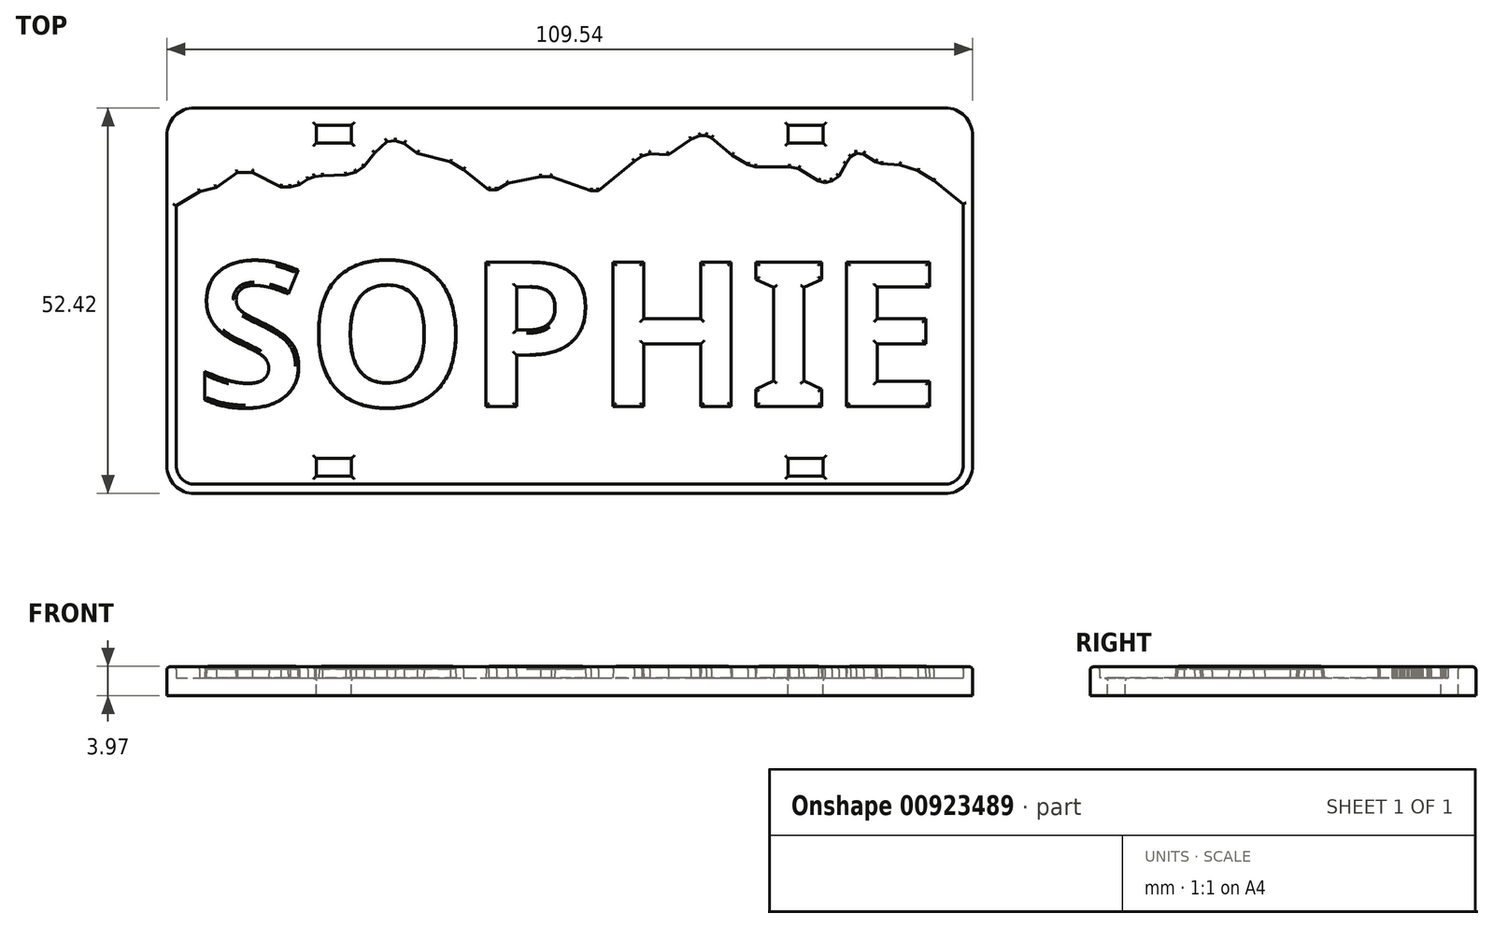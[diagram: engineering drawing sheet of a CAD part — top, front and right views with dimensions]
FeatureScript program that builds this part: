
annotation { "Feature Type Name" : "Feature", "Feature Type Description" : "" }
export const myFeature = defineFeature(function(context is Context, id is Id, definition is map)
    precondition{}
    {
        {
            var Q0;
            Q0=qCreatedBy(makeId("Top.planeOp"),FACE);
            var sketch = newSketch(context, id + "F0", { "sketchPlane" : qUnion([Q0])});
            skLineSegment(sketch, "E0", {"start": v(54.77, -22.46) * mm, "end": v(54.77, 22.46) * mm});
            skArc(sketch, "E1", {"start": v(54.77, 22.46) * mm, "mid": v(53.68, 25.11) * mm, "end": v(51.02, 26.21) * mm});
            skLineSegment(sketch, "E2", {"start": v(51.02, 26.21) * mm, "end": v(-51.02, 26.21) * mm});
            skArc(sketch, "E3", {"start": v(-51.02, 26.21) * mm, "mid": v(-53.68, 25.11) * mm, "end": v(-54.77, 22.46) * mm});
            skLineSegment(sketch, "E4", {"start": v(-54.77, 22.46) * mm, "end": v(-54.77, -22.46) * mm});
            skArc(sketch, "E5", {"start": v(-54.77, -22.46) * mm, "mid": v(-53.54, -25.24) * mm, "end": v(-50.64, -26.2) * mm});
            skLineSegment(sketch, "E6", {"start": v(-50.64, -26.2) * mm, "end": v(51.04, -26.2) * mm});
            skArc(sketch, "E7", {"start": v(51.02, -26.21) * mm, "mid": v(53.68, -25.11) * mm, "end": v(54.77, -22.46) * mm});
            skLineSegment(sketch, "E8", {"start": v(-54.77, 12.13) * mm, "end": v(-50.31, 14.84) * mm});
            skLineSegment(sketch, "E9", {"start": v(-50.31, 14.84) * mm, "end": v(-48.06, 15.4) * mm});
            skLineSegment(sketch, "E10", {"start": v(-48.06, 15.4) * mm, "end": v(-45.2, 17.44) * mm});
            skLineSegment(sketch, "E11", {"start": v(-45.2, 17.44) * mm, "end": v(-43.14, 17.44) * mm});
            skLineSegment(sketch, "E12", {"start": v(-43.14, 17.44) * mm, "end": v(-39.3, 15.5) * mm});
            skLineSegment(sketch, "E13", {"start": v(-39.3, 15.5) * mm, "end": v(-38.03, 15.49) * mm});
            skLineSegment(sketch, "E14", {"start": v(-38.03, 15.49) * mm, "end": v(-36.75, 15.8) * mm});
            skLineSegment(sketch, "E15", {"start": v(-36.75, 15.8) * mm, "end": v(-35.57, 16.54) * mm});
            skLineSegment(sketch, "E16", {"start": v(-35.57, 16.54) * mm, "end": v(-34.73, 16.88) * mm});
            skLineSegment(sketch, "E17", {"start": v(-34.73, 16.88) * mm, "end": v(-33.6, 17.01) * mm});
            skLineSegment(sketch, "E18", {"start": v(-33.6, 17.01) * mm, "end": v(-30.43, 17.11) * mm});
            skLineSegment(sketch, "E19", {"start": v(-29.05, 17.5) * mm, "end": v(-27.98, 18.27) * mm});
            skLineSegment(sketch, "E20", {"start": v(-27.98, 18.27) * mm, "end": v(-26.53, 20.14) * mm});
            skLineSegment(sketch, "E21", {"start": v(-26.53, 20.14) * mm, "end": v(-24.88, 21.63) * mm});
            skLineSegment(sketch, "E22", {"start": v(-24.88, 21.63) * mm, "end": v(-23.73, 21.77) * mm});
            skLineSegment(sketch, "E23", {"start": v(-22.5, 21.4) * mm, "end": v(-20.72, 20.04) * mm});
            skLineSegment(sketch, "E24", {"start": v(-16.23, 18.87) * mm, "end": v(-14.45, 17.85) * mm});
            skLineSegment(sketch, "E25", {"start": v(-14.45, 17.85) * mm, "end": v(-11.02, 15.1) * mm});
            skLineSegment(sketch, "E26", {"start": v(-11.02, 15.1) * mm, "end": v(-9.93, 15.1) * mm});
            skLineSegment(sketch, "E27", {"start": v(-9.93, 15.1) * mm, "end": v(-8.4, 15.96) * mm});
            skLineSegment(sketch, "E28", {"start": v(-8.4, 15.96) * mm, "end": v(-3.94, 16.85) * mm});
            skLineSegment(sketch, "E29", {"start": v(-3.94, 16.85) * mm, "end": v(-2.54, 16.85) * mm});
            skLineSegment(sketch, "E30", {"start": v(-2.54, 16.85) * mm, "end": v(2.9, 14.97) * mm});
            skLineSegment(sketch, "E31", {"start": v(2.9, 14.97) * mm, "end": v(3.92, 14.97) * mm});
            skLineSegment(sketch, "E32", {"start": v(3.92, 14.97) * mm, "end": v(8.8, 18.97) * mm});
            skLineSegment(sketch, "E33", {"start": v(8.8, 18.97) * mm, "end": v(9.82, 19.64) * mm});
            skLineSegment(sketch, "E34", {"start": v(9.82, 19.64) * mm, "end": v(10.9, 19.97) * mm});
            skLineSegment(sketch, "E35", {"start": v(10.9, 19.97) * mm, "end": v(13.43, 19.86) * mm});
            skLineSegment(sketch, "E36", {"start": v(16.5, 21.96) * mm, "end": v(17.71, 22.42) * mm});
            skLineSegment(sketch, "E37", {"start": v(17.71, 22.42) * mm, "end": v(18.56, 22.45) * mm});
            skLineSegment(sketch, "E38", {"start": v(18.56, 22.45) * mm, "end": v(19.28, 22.13) * mm});
            skLineSegment(sketch, "E39", {"start": v(19.28, 22.13) * mm, "end": v(22.05, 19.8) * mm});
            skLineSegment(sketch, "E40", {"start": v(22.05, 19.8) * mm, "end": v(24.2, 18.5) * mm});
            skLineSegment(sketch, "E41", {"start": v(24.2, 18.5) * mm, "end": v(25.23, 18.2) * mm});
            skLineSegment(sketch, "E42", {"start": v(25.23, 18.2) * mm, "end": v(29.85, 18.2) * mm});
            skLineSegment(sketch, "E43", {"start": v(29.85, 18.2) * mm, "end": v(31.13, 17.95) * mm});
            skLineSegment(sketch, "E44", {"start": v(31.13, 17.95) * mm, "end": v(33.84, 16.27) * mm});
            skLineSegment(sketch, "E45", {"start": v(33.84, 16.27) * mm, "end": v(34.73, 16.06) * mm});
            skLineSegment(sketch, "E46", {"start": v(34.73, 16.06) * mm, "end": v(35.67, 16.3) * mm});
            skLineSegment(sketch, "E47", {"start": v(35.67, 16.3) * mm, "end": v(36.58, 16.95) * mm});
            skLineSegment(sketch, "E48", {"start": v(36.58, 16.95) * mm, "end": v(37.58, 18.67) * mm});
            skLineSegment(sketch, "E49", {"start": v(38.22, 19.58) * mm, "end": v(38.96, 20.06) * mm});
            skLineSegment(sketch, "E50", {"start": v(38.96, 20.06) * mm, "end": v(39.94, 19.92) * mm});
            skLineSegment(sketch, "E51", {"start": v(41.58, 18.88) * mm, "end": v(42.4, 18.61) * mm});
            skLineSegment(sketch, "E52", {"start": v(42.4, 18.61) * mm, "end": v(44.9, 18.47) * mm});
            skLineSegment(sketch, "E53", {"start": v(44.9, 18.47) * mm, "end": v(47.31, 17.68) * mm});
            skLineSegment(sketch, "E54", {"start": v(47.31, 17.68) * mm, "end": v(49.47, 16.33) * mm});
            skLineSegment(sketch, "E55", {"start": v(49.47, 16.33) * mm, "end": v(51.88, 14.42) * mm});
            skLineSegment(sketch, "E56", {"start": v(51.88, 14.42) * mm, "end": v(53.78, 12.92) * mm});
            skLineSegment(sketch, "E57", {"start": v(53.78, 12.92) * mm, "end": v(54.77, 12.06) * mm});
            skLineSegment(sketch, "E58", {"start": v(-20.72, 20.04) * mm, "end": v(-16.23, 18.87) * mm});
            skLineSegment(sketch, "E59", {"start": v(16.5, 21.96) * mm, "end": v(13.43, 19.86) * mm});
            skLineSegment(sketch, "E60", {"start": v(-22.5, 21.4) * mm, "end": v(-23.73, 21.77) * mm});
            skLineSegment(sketch, "E61", {"start": v(-29.05, 17.5) * mm, "end": v(-30.43, 17.11) * mm});
            skLineSegment(sketch, "E62", {"start": v(37.58, 18.67) * mm, "end": v(38.22, 19.58) * mm});
            skLineSegment(sketch, "E63", {"start": v(41.58, 18.88) * mm, "end": v(39.94, 19.92) * mm});
            skSolve(sketch);
        }
        {
            var Q0;
            Q0=qCreatedBy(makeId("Top.planeOp"),FACE);
            var sketch = newSketch(context, id + "F1", { "sketchPlane" : qUnion([Q0])});
            skLineSegment(sketch, "E64", {"start": v(54.77, -22.46) * mm, "end": v(54.77, 22.46) * mm});
            skArc(sketch, "E65", {"start": v(54.77, 22.46) * mm, "mid": v(53.68, 25.11) * mm, "end": v(51.02, 26.21) * mm});
            skLineSegment(sketch, "E66", {"start": v(51.02, 26.21) * mm, "end": v(-51.02, 26.21) * mm});
            skArc(sketch, "E67", {"start": v(-51.02, 26.21) * mm, "mid": v(-53.68, 25.11) * mm, "end": v(-54.77, 22.46) * mm});
            skLineSegment(sketch, "E68", {"start": v(-54.77, 22.46) * mm, "end": v(-54.77, -22.46) * mm});
            skArc(sketch, "E69", {"start": v(-54.77, -22.46) * mm, "mid": v(-53.68, -25.11) * mm, "end": v(-51.02, -26.21) * mm});
            skLineSegment(sketch, "E70", {"start": v(-51.02, -26.21) * mm, "end": v(51.02, -26.21) * mm});
            skArc(sketch, "E71", {"start": v(51.02, -26.21) * mm, "mid": v(53.68, -25.11) * mm, "end": v(54.77, -22.46) * mm});
            skLineSegment(sketch, "E72.0", {"start": v(50.96, 24.94) * mm, "end": v(-50.96, 24.94) * mm, "construction": true});
            skLineSegment(sketch, "E72.1", {"start": v(53.5, -22.4) * mm, "end": v(53.5, 22.4) * mm, "construction": true});
            skLineSegment(sketch, "E72.2", {"start": v(-50.96, -24.94) * mm, "end": v(50.96, -24.94) * mm, "construction": true});
            skLineSegment(sketch, "E72.3", {"start": v(-53.5, 22.4) * mm, "end": v(-53.5, -22.4) * mm, "construction": true});
            skPoint(sketch, "E73.visualSharp", {"position": v(-53.5, 24.94) * mm});
            skArc(sketch, "E73.filletArc", {"start": v(-50.96, 24.94) * mm, "mid": v(-52.76, 24.2) * mm, "end": v(-53.5, 22.4) * mm, "construction": true});
            skPoint(sketch, "E74.visualSharp", {"position": v(-53.5, -24.94) * mm});
            skArc(sketch, "E74.filletArc", {"start": v(-53.5, -22.4) * mm, "mid": v(-52.76, -24.2) * mm, "end": v(-50.96, -24.94) * mm, "construction": true});
            skPoint(sketch, "E75.visualSharp", {"position": v(53.5, -24.94) * mm});
            skArc(sketch, "E75.filletArc", {"start": v(50.96, -24.94) * mm, "mid": v(52.76, -24.2) * mm, "end": v(53.5, -22.4) * mm, "construction": true});
            skPoint(sketch, "E76.visualSharp", {"position": v(53.5, 24.94) * mm});
            skArc(sketch, "E76.filletArc", {"start": v(53.5, 22.4) * mm, "mid": v(52.76, 24.2) * mm, "end": v(50.96, 24.94) * mm, "construction": true});
            skSolve(sketch);
        }
        {
            var Q0;
            {var subQ3=sQuery(id+"F0.wireOp",EDGE,"E1");Q0=makeQuery(id+"F0.imprint","IMPRINT",FACE,{"disambiguationData":[TD([[makeQuery(id+"F0.imprint","IMPRINT",EDGE,{"derivedFrom":subQ3}),1.0]])]});}
            extrude(context, id + "F2", {"entities" : qUnion([Q0]), "depth" : 1.52 * mm, "offsetDistance" : 25.4 * mm});
        }
        {
            var Q0;
            Q0=qSketchRegion(id+"F1",true);
            extrude(context, id + "F3", {"entities" : qUnion([Q0]), "operationType" : NewBodyOperationType.ADD, "oppositeDirection" : true, "depth" : 2.38 * mm, "offsetDistance" : 25.4 * mm});
        }
        {
            var Q0;
            {var subQ58=sQuery(id+"F0.wireOp",EDGE,"E0");var subQ59=sQuery(id+"F1.wireOp",EDGE,"E64");var subQ60=sQuery(id+"F1.wireOp",EDGE,"E65");var subQ61=sQuery(id+"F1.wireOp",EDGE,"E68");var subQ62=sQuery(id+"F1.wireOp",EDGE,"E69");var subQ63=sQuery(id+"F1.wireOp",EDGE,"E70");var subQ64=sQuery(id+"F1.wireOp",EDGE,"E71");Q0=makeQuery(id+"F3.boolean.opBoolean","SPLIT",FACE,{"disambiguationData":[TD([makeQuery(id+"F2.opExtrude","SWEPT_FACE",FACE,{"disambiguationData":[OSD([subQ58])]})])],"derivedFrom":makeQuery(id+"F3.opExtrude","CAP_FACE",FACE,{"disambiguationData":[OSD([subQ59,subQ60,sQuery(id+"F1.wireOp",EDGE,"E66"),sQuery(id+"F1.wireOp",EDGE,"E67"),subQ61,subQ62,subQ63,subQ64])],"isStart":true})});}
            var sketch = newSketch(context, id + "F4", { "sketchPlane" : qUnion([Q0])});
            skLineSegment(sketch, "E77", {"start": v(54.77, -22.46) * mm, "end": v(54.77, 12.06) * mm});
            skLineSegment(sketch, "E78", {"start": v(-54.77, 12.13) * mm, "end": v(-54.77, -22.46) * mm});
            skArc(sketch, "E79", {"start": v(-54.77, -22.46) * mm, "mid": v(-53.68, -25.11) * mm, "end": v(-51.02, -26.21) * mm});
            skLineSegment(sketch, "E80", {"start": v(-51.02, -26.21) * mm, "end": v(51.02, -26.21) * mm});
            skArc(sketch, "E81", {"start": v(51.02, -26.21) * mm, "mid": v(53.68, -25.11) * mm, "end": v(54.77, -22.46) * mm});
            skLineSegment(sketch, "E82.1", {"start": v(53.5, -22.4) * mm, "end": v(53.5, 13.14) * mm});
            skLineSegment(sketch, "E82.2", {"start": v(-50.96, -24.94) * mm, "end": v(50.96, -24.94) * mm});
            skLineSegment(sketch, "E82.3", {"start": v(-53.5, 12.9) * mm, "end": v(-53.5, -22.4) * mm});
            skPoint(sketch, "E83.visualSharp", {"position": v(-53.5, 24.94) * mm});
            skPoint(sketch, "E84.visualSharp", {"position": v(-53.5, -24.94) * mm});
            skArc(sketch, "E84.filletArc", {"start": v(-53.5, -22.4) * mm, "mid": v(-52.76, -24.2) * mm, "end": v(-50.96, -24.94) * mm});
            skPoint(sketch, "E85.visualSharp", {"position": v(53.5, -24.94) * mm});
            skArc(sketch, "E85.filletArc", {"start": v(50.96, -24.94) * mm, "mid": v(52.76, -24.2) * mm, "end": v(53.5, -22.4) * mm});
            skPoint(sketch, "E86.visualSharp", {"position": v(53.5, 24.94) * mm});
            skLineSegment(sketch, "E87", {"start": v(-54.77, 12.13) * mm, "end": v(-53.5, 12.9) * mm});
            skLineSegment(sketch, "E88", {"start": v(53.5, 13.14) * mm, "end": v(53.78, 12.92) * mm});
            skLineSegment(sketch, "E89", {"start": v(53.78, 12.92) * mm, "end": v(54.77, 12.06) * mm});
            skSolve(sketch);
        }
        {
            var Q0;
            Q0=qSketchRegion(id+"F4",true);
            extrude(context, id + "F5", {"entities" : qUnion([Q0]), "operationType" : NewBodyOperationType.ADD, "depth" : 1.52 * mm, "offsetDistance" : 25.4 * mm});
        }
        {
            var Q0;
            Q0=makeQuery(id+"F5.boolean.opBoolean","MERGE",FACE,{"derivedFrom":[makeQuery(id+"F2.opExtrude","CAP_FACE",FACE,{"disambiguationData":[OSD([sQuery(id+"F0.wireOp",EDGE,"E0"),sQuery(id+"F0.wireOp",EDGE,"E1"),sQuery(id+"F0.wireOp",EDGE,"E2"),sQuery(id+"F0.wireOp",EDGE,"E3"),sQuery(id+"F0.wireOp",EDGE,"E4"),sQuery(id+"F0.wireOp",EDGE,"E8"),sQuery(id+"F0.wireOp",EDGE,"E9"),sQuery(id+"F0.wireOp",EDGE,"E10"),sQuery(id+"F0.wireOp",EDGE,"E11"),sQuery(id+"F0.wireOp",EDGE,"E12"),sQuery(id+"F0.wireOp",EDGE,"E13"),sQuery(id+"F0.wireOp",EDGE,"E14"),sQuery(id+"F0.wireOp",EDGE,"E15"),sQuery(id+"F0.wireOp",EDGE,"E16"),sQuery(id+"F0.wireOp",EDGE,"E17"),sQuery(id+"F0.wireOp",EDGE,"E18"),sQuery(id+"F0.wireOp",EDGE,"7b9f405e-0691-426e-9c9e-a5372cf0836a"),sQuery(id+"F0.wireOp",EDGE,"E19"),sQuery(id+"F0.wireOp",EDGE,"E20"),sQuery(id+"F0.wireOp",EDGE,"E21"),sQuery(id+"F0.wireOp",EDGE,"E22"),sQuery(id+"F0.wireOp",EDGE,"b3dec5b1-662c-4d50-a13c-af7b7760114a"),sQuery(id+"F0.wireOp",EDGE,"E23"),sQuery(id+"F0.wireOp",EDGE,"4d9ee76e-0833-4cdc-b1a8-2d4ce76e6521"),sQuery(id+"F0.wireOp",EDGE,"E24"),sQuery(id+"F0.wireOp",EDGE,"E25"),sQuery(id+"F0.wireOp",EDGE,"E26"),sQuery(id+"F0.wireOp",EDGE,"E27"),sQuery(id+"F0.wireOp",EDGE,"E28"),sQuery(id+"F0.wireOp",EDGE,"E29"),sQuery(id+"F0.wireOp",EDGE,"E30"),sQuery(id+"F0.wireOp",EDGE,"E31"),sQuery(id+"F0.wireOp",EDGE,"E32"),sQuery(id+"F0.wireOp",EDGE,"E33"),sQuery(id+"F0.wireOp",EDGE,"E34"),sQuery(id+"F0.wireOp",EDGE,"E35"),sQuery(id+"F0.wireOp",EDGE,"55551997-bb9e-4b94-90c5-def3cb147476"),sQuery(id+"F0.wireOp",EDGE,"E36"),sQuery(id+"F0.wireOp",EDGE,"E37"),sQuery(id+"F0.wireOp",EDGE,"E38"),sQuery(id+"F0.wireOp",EDGE,"E39"),sQuery(id+"F0.wireOp",EDGE,"E40"),sQuery(id+"F0.wireOp",EDGE,"E41"),sQuery(id+"F0.wireOp",EDGE,"E42"),sQuery(id+"F0.wireOp",EDGE,"E43"),sQuery(id+"F0.wireOp",EDGE,"E44"),sQuery(id+"F0.wireOp",EDGE,"E45"),sQuery(id+"F0.wireOp",EDGE,"E46"),sQuery(id+"F0.wireOp",EDGE,"E47"),sQuery(id+"F0.wireOp",EDGE,"E48"),sQuery(id+"F0.wireOp",EDGE,"513b7cbe-d979-4e22-b277-f3c42ccdbda1"),sQuery(id+"F0.wireOp",EDGE,"E49"),sQuery(id+"F0.wireOp",EDGE,"E50"),sQuery(id+"F0.wireOp",EDGE,"0d842e13-672c-40e3-aae4-28923e78d4e0"),sQuery(id+"F0.wireOp",EDGE,"E51"),sQuery(id+"F0.wireOp",EDGE,"E52"),sQuery(id+"F0.wireOp",EDGE,"E53"),sQuery(id+"F0.wireOp",EDGE,"E54"),sQuery(id+"F0.wireOp",EDGE,"E55"),sQuery(id+"F0.wireOp",EDGE,"E56"),sQuery(id+"F0.wireOp",EDGE,"E57")])],"isStart":false}),makeQuery(id+"F5.opExtrude","CAP_FACE",FACE,{"disambiguationData":[OSD([sQuery(id+"F4.wireOp",EDGE,"E77"),sQuery(id+"F4.wireOp",EDGE,"E78"),sQuery(id+"F4.wireOp",EDGE,"E79"),sQuery(id+"F4.wireOp",EDGE,"E80"),sQuery(id+"F4.wireOp",EDGE,"E81"),sQuery(id+"F4.wireOp",EDGE,"E82.1"),sQuery(id+"F4.wireOp",EDGE,"E82.2"),sQuery(id+"F4.wireOp",EDGE,"E82.3"),sQuery(id+"F4.wireOp",EDGE,"E84.filletArc"),sQuery(id+"F4.wireOp",EDGE,"E85.filletArc"),sQuery(id+"F4.wireOp",EDGE,"E87"),sQuery(id+"F4.wireOp",EDGE,"E88"),sQuery(id+"F4.wireOp",EDGE,"E89")])],"isStart":false})]});
            var sketch = newSketch(context, id + "F6", { "sketchPlane" : qUnion([Q0])});
            skLineSegment(sketch, "E90.bottom", {"start": v(-34.45, 23.83) * mm, "end": v(-29.7, 23.83) * mm});
            skLineSegment(sketch, "E90.top", {"start": v(-34.45, 21.45) * mm, "end": v(-29.7, 21.45) * mm});
            skLineSegment(sketch, "E90.left", {"start": v(-34.45, 23.83) * mm, "end": v(-34.45, 21.45) * mm});
            skLineSegment(sketch, "E90.right", {"start": v(-29.7, 23.83) * mm, "end": v(-29.7, 21.45) * mm});
            skLineSegment(sketch, "E91", {"start": v(0, 26.21) * mm, "end": v(0, -26.21) * mm, "construction": true});
            skLineSegment(sketch, "E92.MirrorCS", {"start": v(34.45, 23.83) * mm, "end": v(34.45, 21.45) * mm});
            skLineSegment(sketch, "E93.MirrorCS", {"start": v(29.7, 23.83) * mm, "end": v(29.7, 21.45) * mm});
            skLineSegment(sketch, "E94.MirrorCS", {"start": v(34.45, 21.45) * mm, "end": v(29.7, 21.45) * mm});
            skLineSegment(sketch, "E95.MirrorCS", {"start": v(34.45, 23.83) * mm, "end": v(29.7, 23.83) * mm});
            skLineSegment(sketch, "E96", {"start": v(0, 0) * mm, "end": v(-59.23, 0) * mm, "construction": true});
            skLineSegment(sketch, "E97", {"start": v(0, 0) * mm, "end": v(56.47, 0) * mm, "construction": true});
            skLineSegment(sketch, "E98.MirrorCS", {"start": v(-34.45, -23.83) * mm, "end": v(-29.7, -23.83) * mm});
            skLineSegment(sketch, "E99.MirrorCS", {"start": v(-34.45, -23.83) * mm, "end": v(-34.45, -21.45) * mm});
            skLineSegment(sketch, "E100.MirrorCS", {"start": v(-34.45, -21.45) * mm, "end": v(-29.7, -21.45) * mm});
            skLineSegment(sketch, "E101.MirrorCS", {"start": v(-29.7, -23.83) * mm, "end": v(-29.7, -21.45) * mm});
            skLineSegment(sketch, "E102.MirrorCS", {"start": v(29.7, -23.83) * mm, "end": v(29.7, -21.45) * mm});
            skLineSegment(sketch, "E103.MirrorCS", {"start": v(34.45, -23.83) * mm, "end": v(29.7, -23.83) * mm});
            skLineSegment(sketch, "E104.MirrorCS", {"start": v(34.45, -23.83) * mm, "end": v(34.45, -21.45) * mm});
            skLineSegment(sketch, "E105.MirrorCS", {"start": v(34.45, -21.45) * mm, "end": v(29.7, -21.45) * mm});
            skSolve(sketch);
        }
        {
            var Q0;
            Q0=qSketchRegion(id+"F6",true);
            extrude(context, id + "F7", {"entities" : qUnion([Q0]), "operationType" : NewBodyOperationType.REMOVE, "endBound" : BoundingType.THROUGH_ALL, "oppositeDirection" : true, "depth" : 25.4 * mm, "offsetDistance" : 25.4 * mm});
        }
        {
            var Q0;
            Q0=makeQuery(id+"F3.opExtrude","CAP_FACE",FACE,{"disambiguationData":[OSD([sQuery(id+"F1.wireOp",EDGE,"E64"),sQuery(id+"F1.wireOp",EDGE,"E65"),sQuery(id+"F1.wireOp",EDGE,"E66"),sQuery(id+"F1.wireOp",EDGE,"E67"),sQuery(id+"F1.wireOp",EDGE,"E68"),sQuery(id+"F1.wireOp",EDGE,"E69"),sQuery(id+"F1.wireOp",EDGE,"E70"),sQuery(id+"F1.wireOp",EDGE,"E71")])],"isStart":true});
            var sketch = newSketch(context, id + "F8", { "sketchPlane" : qUnion([Q0])});
            skText(sketch, "E106", { "text": "SOPHIE", "fontName": "NotoSans-Bold.ttf"});
            const initialGuessF8  = {"E106": [-0.0509, -0.01437, 1, 0, 0.0198]};
            skSetInitialGuess(sketch, initialGuessF8);
            skSolve(sketch);
        }
        {
            var Q0;
            Q0=qSketchRegion(id+"F8",true);
            extrude(context, id + "F9", {"entities" : qUnion([Q0]), "operationType" : NewBodyOperationType.ADD, "depth" : 1.59 * mm, "offsetDistance" : 25.4 * mm, "hasDraft" : true, "draftAngle" : 3 * degree, "draftPullDirection" : true});
        }
        {
            var Q0;
            Q0=makeQuery(id+"F5.boolean.opBoolean","MERGE",FACE,{"derivedFrom":[makeQuery(id+"F2.opExtrude","CAP_FACE",FACE,{"disambiguationData":[OSD([sQuery(id+"F0.wireOp",EDGE,"E0"),sQuery(id+"F0.wireOp",EDGE,"E1"),sQuery(id+"F0.wireOp",EDGE,"E2"),sQuery(id+"F0.wireOp",EDGE,"E3"),sQuery(id+"F0.wireOp",EDGE,"E4"),sQuery(id+"F0.wireOp",EDGE,"E8"),sQuery(id+"F0.wireOp",EDGE,"E9"),sQuery(id+"F0.wireOp",EDGE,"E10"),sQuery(id+"F0.wireOp",EDGE,"E11"),sQuery(id+"F0.wireOp",EDGE,"E12"),sQuery(id+"F0.wireOp",EDGE,"E13"),sQuery(id+"F0.wireOp",EDGE,"E14"),sQuery(id+"F0.wireOp",EDGE,"E15"),sQuery(id+"F0.wireOp",EDGE,"E16"),sQuery(id+"F0.wireOp",EDGE,"E17"),sQuery(id+"F0.wireOp",EDGE,"E18"),sQuery(id+"F0.wireOp",EDGE,"7b9f405e-0691-426e-9c9e-a5372cf0836a"),sQuery(id+"F0.wireOp",EDGE,"E19"),sQuery(id+"F0.wireOp",EDGE,"E20"),sQuery(id+"F0.wireOp",EDGE,"E21"),sQuery(id+"F0.wireOp",EDGE,"E22"),sQuery(id+"F0.wireOp",EDGE,"b3dec5b1-662c-4d50-a13c-af7b7760114a"),sQuery(id+"F0.wireOp",EDGE,"E23"),sQuery(id+"F0.wireOp",EDGE,"4d9ee76e-0833-4cdc-b1a8-2d4ce76e6521"),sQuery(id+"F0.wireOp",EDGE,"E24"),sQuery(id+"F0.wireOp",EDGE,"E25"),sQuery(id+"F0.wireOp",EDGE,"E26"),sQuery(id+"F0.wireOp",EDGE,"E27"),sQuery(id+"F0.wireOp",EDGE,"E28"),sQuery(id+"F0.wireOp",EDGE,"E29"),sQuery(id+"F0.wireOp",EDGE,"E30"),sQuery(id+"F0.wireOp",EDGE,"E31"),sQuery(id+"F0.wireOp",EDGE,"E32"),sQuery(id+"F0.wireOp",EDGE,"E33"),sQuery(id+"F0.wireOp",EDGE,"E34"),sQuery(id+"F0.wireOp",EDGE,"E35"),sQuery(id+"F0.wireOp",EDGE,"55551997-bb9e-4b94-90c5-def3cb147476"),sQuery(id+"F0.wireOp",EDGE,"E36"),sQuery(id+"F0.wireOp",EDGE,"E37"),sQuery(id+"F0.wireOp",EDGE,"E38"),sQuery(id+"F0.wireOp",EDGE,"E39"),sQuery(id+"F0.wireOp",EDGE,"E40"),sQuery(id+"F0.wireOp",EDGE,"E41"),sQuery(id+"F0.wireOp",EDGE,"E42"),sQuery(id+"F0.wireOp",EDGE,"E43"),sQuery(id+"F0.wireOp",EDGE,"E44"),sQuery(id+"F0.wireOp",EDGE,"E45"),sQuery(id+"F0.wireOp",EDGE,"E46"),sQuery(id+"F0.wireOp",EDGE,"E47"),sQuery(id+"F0.wireOp",EDGE,"E48"),sQuery(id+"F0.wireOp",EDGE,"513b7cbe-d979-4e22-b277-f3c42ccdbda1"),sQuery(id+"F0.wireOp",EDGE,"E49"),sQuery(id+"F0.wireOp",EDGE,"E50"),sQuery(id+"F0.wireOp",EDGE,"0d842e13-672c-40e3-aae4-28923e78d4e0"),sQuery(id+"F0.wireOp",EDGE,"E51"),sQuery(id+"F0.wireOp",EDGE,"E52"),sQuery(id+"F0.wireOp",EDGE,"E53"),sQuery(id+"F0.wireOp",EDGE,"E54"),sQuery(id+"F0.wireOp",EDGE,"E55"),sQuery(id+"F0.wireOp",EDGE,"E56"),sQuery(id+"F0.wireOp",EDGE,"E57")])],"isStart":false}),makeQuery(id+"F5.opExtrude","CAP_FACE",FACE,{"disambiguationData":[OSD([sQuery(id+"F4.wireOp",EDGE,"E77"),sQuery(id+"F4.wireOp",EDGE,"E78"),sQuery(id+"F4.wireOp",EDGE,"E79"),sQuery(id+"F4.wireOp",EDGE,"E80"),sQuery(id+"F4.wireOp",EDGE,"E81"),sQuery(id+"F4.wireOp",EDGE,"E82.1"),sQuery(id+"F4.wireOp",EDGE,"E82.2"),sQuery(id+"F4.wireOp",EDGE,"E82.3"),sQuery(id+"F4.wireOp",EDGE,"E84.filletArc"),sQuery(id+"F4.wireOp",EDGE,"E85.filletArc"),sQuery(id+"F4.wireOp",EDGE,"E87"),sQuery(id+"F4.wireOp",EDGE,"E88"),sQuery(id+"F4.wireOp",EDGE,"E89")])],"isStart":false})]});
            var Q1;
            {var subQ0=sQuery(id+"F1.wireOp",EDGE,"E64");var subQ1=sQuery(id+"F1.wireOp",EDGE,"E68");var subQ2=sQuery(id+"F1.wireOp",EDGE,"E69");var subQ3=sQuery(id+"F1.wireOp",EDGE,"E70");var subQ4=sQuery(id+"F1.wireOp",EDGE,"E71");Q1=makeQuery(id+"F7.boolean.opBoolean","INTERSECT",EDGE,{"derivedFrom":[makeQuery(id+"F3.boolean.opBoolean","SPLIT",FACE,{"disambiguationData":[TD([makeQuery(id+"F2.opExtrude","SWEPT_FACE",FACE,{"disambiguationData":[OSD([sQuery(id+"F0.wireOp",EDGE,"E0")])]})])],"derivedFrom":makeQuery(id+"F3.opExtrude","CAP_FACE",FACE,{"disambiguationData":[OSD([subQ0,sQuery(id+"F1.wireOp",EDGE,"E65"),sQuery(id+"F1.wireOp",EDGE,"E66"),sQuery(id+"F1.wireOp",EDGE,"E67"),subQ1,subQ2,subQ3,subQ4])],"isStart":true})}),makeQuery(id+"F7.opExtrude","SWEPT_FACE",FACE,{"disambiguationData":[OSD([sQuery(id+"F6.wireOp",EDGE,"E100.MirrorCS")])]})]});}
            var Q2;
            {var subQ0=sQuery(id+"F1.wireOp",EDGE,"E64");var subQ1=sQuery(id+"F1.wireOp",EDGE,"E68");var subQ2=sQuery(id+"F1.wireOp",EDGE,"E69");var subQ3=sQuery(id+"F1.wireOp",EDGE,"E70");var subQ4=sQuery(id+"F1.wireOp",EDGE,"E71");Q2=makeQuery(id+"F7.boolean.opBoolean","INTERSECT",EDGE,{"derivedFrom":[makeQuery(id+"F3.boolean.opBoolean","SPLIT",FACE,{"disambiguationData":[TD([makeQuery(id+"F2.opExtrude","SWEPT_FACE",FACE,{"disambiguationData":[OSD([sQuery(id+"F0.wireOp",EDGE,"E0")])]})])],"derivedFrom":makeQuery(id+"F3.opExtrude","CAP_FACE",FACE,{"disambiguationData":[OSD([subQ0,sQuery(id+"F1.wireOp",EDGE,"E65"),sQuery(id+"F1.wireOp",EDGE,"E66"),sQuery(id+"F1.wireOp",EDGE,"E67"),subQ1,subQ2,subQ3,subQ4])],"isStart":true})}),makeQuery(id+"F7.opExtrude","SWEPT_FACE",FACE,{"disambiguationData":[OSD([sQuery(id+"F6.wireOp",EDGE,"E99.MirrorCS")])]})]});}
            var Q3;
            {var subQ0=sQuery(id+"F1.wireOp",EDGE,"E64");var subQ1=sQuery(id+"F1.wireOp",EDGE,"E68");var subQ2=sQuery(id+"F1.wireOp",EDGE,"E69");var subQ3=sQuery(id+"F1.wireOp",EDGE,"E70");var subQ4=sQuery(id+"F1.wireOp",EDGE,"E71");Q3=makeQuery(id+"F7.boolean.opBoolean","INTERSECT",EDGE,{"derivedFrom":[makeQuery(id+"F3.boolean.opBoolean","SPLIT",FACE,{"disambiguationData":[TD([makeQuery(id+"F2.opExtrude","SWEPT_FACE",FACE,{"disambiguationData":[OSD([sQuery(id+"F0.wireOp",EDGE,"E0")])]})])],"derivedFrom":makeQuery(id+"F3.opExtrude","CAP_FACE",FACE,{"disambiguationData":[OSD([subQ0,sQuery(id+"F1.wireOp",EDGE,"E65"),sQuery(id+"F1.wireOp",EDGE,"E66"),sQuery(id+"F1.wireOp",EDGE,"E67"),subQ1,subQ2,subQ3,subQ4])],"isStart":true})}),makeQuery(id+"F7.opExtrude","SWEPT_FACE",FACE,{"disambiguationData":[OSD([sQuery(id+"F6.wireOp",EDGE,"E98.MirrorCS")])]})]});}
            var Q4;
            {var subQ0=sQuery(id+"F1.wireOp",EDGE,"E64");var subQ1=sQuery(id+"F1.wireOp",EDGE,"E68");var subQ2=sQuery(id+"F1.wireOp",EDGE,"E69");var subQ3=sQuery(id+"F1.wireOp",EDGE,"E70");var subQ4=sQuery(id+"F1.wireOp",EDGE,"E71");Q4=makeQuery(id+"F7.boolean.opBoolean","INTERSECT",EDGE,{"derivedFrom":[makeQuery(id+"F3.boolean.opBoolean","SPLIT",FACE,{"disambiguationData":[TD([makeQuery(id+"F2.opExtrude","SWEPT_FACE",FACE,{"disambiguationData":[OSD([sQuery(id+"F0.wireOp",EDGE,"E0")])]})])],"derivedFrom":makeQuery(id+"F3.opExtrude","CAP_FACE",FACE,{"disambiguationData":[OSD([subQ0,sQuery(id+"F1.wireOp",EDGE,"E65"),sQuery(id+"F1.wireOp",EDGE,"E66"),sQuery(id+"F1.wireOp",EDGE,"E67"),subQ1,subQ2,subQ3,subQ4])],"isStart":true})}),makeQuery(id+"F7.opExtrude","SWEPT_FACE",FACE,{"disambiguationData":[OSD([sQuery(id+"F6.wireOp",EDGE,"E101.MirrorCS")])]})]});}
            var Q5;
            {var subQ0=sQuery(id+"F1.wireOp",EDGE,"E64");var subQ1=sQuery(id+"F1.wireOp",EDGE,"E68");var subQ2=sQuery(id+"F1.wireOp",EDGE,"E69");var subQ3=sQuery(id+"F1.wireOp",EDGE,"E70");var subQ4=sQuery(id+"F1.wireOp",EDGE,"E71");Q5=makeQuery(id+"F7.boolean.opBoolean","INTERSECT",EDGE,{"derivedFrom":[makeQuery(id+"F3.boolean.opBoolean","SPLIT",FACE,{"disambiguationData":[TD([makeQuery(id+"F2.opExtrude","SWEPT_FACE",FACE,{"disambiguationData":[OSD([sQuery(id+"F0.wireOp",EDGE,"E0")])]})])],"derivedFrom":makeQuery(id+"F3.opExtrude","CAP_FACE",FACE,{"disambiguationData":[OSD([subQ0,sQuery(id+"F1.wireOp",EDGE,"E65"),sQuery(id+"F1.wireOp",EDGE,"E66"),sQuery(id+"F1.wireOp",EDGE,"E67"),subQ1,subQ2,subQ3,subQ4])],"isStart":true})}),makeQuery(id+"F7.opExtrude","SWEPT_FACE",FACE,{"disambiguationData":[OSD([sQuery(id+"F6.wireOp",EDGE,"E102.MirrorCS")])]})]});}
            var Q6;
            {var subQ0=sQuery(id+"F1.wireOp",EDGE,"E64");var subQ1=sQuery(id+"F1.wireOp",EDGE,"E68");var subQ2=sQuery(id+"F1.wireOp",EDGE,"E69");var subQ3=sQuery(id+"F1.wireOp",EDGE,"E70");var subQ4=sQuery(id+"F1.wireOp",EDGE,"E71");Q6=makeQuery(id+"F7.boolean.opBoolean","INTERSECT",EDGE,{"derivedFrom":[makeQuery(id+"F3.boolean.opBoolean","SPLIT",FACE,{"disambiguationData":[TD([makeQuery(id+"F2.opExtrude","SWEPT_FACE",FACE,{"disambiguationData":[OSD([sQuery(id+"F0.wireOp",EDGE,"E0")])]})])],"derivedFrom":makeQuery(id+"F3.opExtrude","CAP_FACE",FACE,{"disambiguationData":[OSD([subQ0,sQuery(id+"F1.wireOp",EDGE,"E65"),sQuery(id+"F1.wireOp",EDGE,"E66"),sQuery(id+"F1.wireOp",EDGE,"E67"),subQ1,subQ2,subQ3,subQ4])],"isStart":true})}),makeQuery(id+"F7.opExtrude","SWEPT_FACE",FACE,{"disambiguationData":[OSD([sQuery(id+"F6.wireOp",EDGE,"E105.MirrorCS")])]})]});}
            var Q7;
            {var subQ0=sQuery(id+"F1.wireOp",EDGE,"E64");var subQ1=sQuery(id+"F1.wireOp",EDGE,"E68");var subQ2=sQuery(id+"F1.wireOp",EDGE,"E69");var subQ3=sQuery(id+"F1.wireOp",EDGE,"E70");var subQ4=sQuery(id+"F1.wireOp",EDGE,"E71");Q7=makeQuery(id+"F7.boolean.opBoolean","INTERSECT",EDGE,{"derivedFrom":[makeQuery(id+"F3.boolean.opBoolean","SPLIT",FACE,{"disambiguationData":[TD([makeQuery(id+"F2.opExtrude","SWEPT_FACE",FACE,{"disambiguationData":[OSD([sQuery(id+"F0.wireOp",EDGE,"E0")])]})])],"derivedFrom":makeQuery(id+"F3.opExtrude","CAP_FACE",FACE,{"disambiguationData":[OSD([subQ0,sQuery(id+"F1.wireOp",EDGE,"E65"),sQuery(id+"F1.wireOp",EDGE,"E66"),sQuery(id+"F1.wireOp",EDGE,"E67"),subQ1,subQ2,subQ3,subQ4])],"isStart":true})}),makeQuery(id+"F7.opExtrude","SWEPT_FACE",FACE,{"disambiguationData":[OSD([sQuery(id+"F6.wireOp",EDGE,"E104.MirrorCS")])]})]});}
            var Q8;
            {var subQ0=sQuery(id+"F1.wireOp",EDGE,"E64");var subQ1=sQuery(id+"F1.wireOp",EDGE,"E68");var subQ2=sQuery(id+"F1.wireOp",EDGE,"E69");var subQ3=sQuery(id+"F1.wireOp",EDGE,"E70");var subQ4=sQuery(id+"F1.wireOp",EDGE,"E71");Q8=makeQuery(id+"F7.boolean.opBoolean","INTERSECT",EDGE,{"derivedFrom":[makeQuery(id+"F3.boolean.opBoolean","SPLIT",FACE,{"disambiguationData":[TD([makeQuery(id+"F2.opExtrude","SWEPT_FACE",FACE,{"disambiguationData":[OSD([sQuery(id+"F0.wireOp",EDGE,"E0")])]})])],"derivedFrom":makeQuery(id+"F3.opExtrude","CAP_FACE",FACE,{"disambiguationData":[OSD([subQ0,sQuery(id+"F1.wireOp",EDGE,"E65"),sQuery(id+"F1.wireOp",EDGE,"E66"),sQuery(id+"F1.wireOp",EDGE,"E67"),subQ1,subQ2,subQ3,subQ4])],"isStart":true})}),makeQuery(id+"F7.opExtrude","SWEPT_FACE",FACE,{"disambiguationData":[OSD([sQuery(id+"F6.wireOp",EDGE,"E103.MirrorCS")])]})]});}
            var Q9;
            Q9=makeQuery(id+"F9.opExtrude","CAP_FACE",FACE,{"disambiguationData":[OSD([sQuery(id+"F8.wireOp",EDGE,"E106.sketch_text.stroke-0"),sQuery(id+"F8.wireOp",EDGE,"E106.sketch_text.stroke-1"),sQuery(id+"F8.wireOp",EDGE,"E106.sketch_text.stroke-2"),sQuery(id+"F8.wireOp",EDGE,"E106.sketch_text.stroke-3"),sQuery(id+"F8.wireOp",EDGE,"E106.sketch_text.stroke-4"),sQuery(id+"F8.wireOp",EDGE,"E106.sketch_text.stroke-5"),sQuery(id+"F8.wireOp",EDGE,"E106.sketch_text.stroke-6"),sQuery(id+"F8.wireOp",EDGE,"E106.sketch_text.stroke-7"),sQuery(id+"F8.wireOp",EDGE,"E106.sketch_text.stroke-8"),sQuery(id+"F8.wireOp",EDGE,"E106.sketch_text.stroke-9"),sQuery(id+"F8.wireOp",EDGE,"E106.sketch_text.stroke-10"),sQuery(id+"F8.wireOp",EDGE,"E106.sketch_text.stroke-11"),sQuery(id+"F8.wireOp",EDGE,"E106.sketch_text.stroke-12"),sQuery(id+"F8.wireOp",EDGE,"E106.sketch_text.stroke-13"),sQuery(id+"F8.wireOp",EDGE,"E106.sketch_text.stroke-14")])],"isStart":false});
            var Q10;
            Q10=makeQuery(id+"F9.opExtrude","CAP_FACE",FACE,{"disambiguationData":[OSD([sQuery(id+"F8.wireOp",EDGE,"E106.sketch_text.stroke-15"),sQuery(id+"F8.wireOp",EDGE,"E106.sketch_text.stroke-16"),sQuery(id+"F8.wireOp",EDGE,"E106.sketch_text.stroke-17"),sQuery(id+"F8.wireOp",EDGE,"E106.sketch_text.stroke-18"),sQuery(id+"F8.wireOp",EDGE,"E106.sketch_text.stroke-19"),sQuery(id+"F8.wireOp",EDGE,"E106.sketch_text.stroke-20"),sQuery(id+"F8.wireOp",EDGE,"E106.sketch_text.stroke-21"),sQuery(id+"F8.wireOp",EDGE,"E106.sketch_text.stroke-22"),sQuery(id+"F8.wireOp",EDGE,"E106.sketch_text.stroke-23"),sQuery(id+"F8.wireOp",EDGE,"E106.sketch_text.stroke-24"),sQuery(id+"F8.wireOp",EDGE,"E106.sketch_text.stroke-25"),sQuery(id+"F8.wireOp",EDGE,"E106.sketch_text.stroke-26"),sQuery(id+"F8.wireOp",EDGE,"E106.sketch_text.stroke-27"),sQuery(id+"F8.wireOp",EDGE,"E106.sketch_text.stroke-28")])],"isStart":false});
            var Q11;
            Q11=makeQuery(id+"F9.opExtrude","CAP_FACE",FACE,{"disambiguationData":[OSD([sQuery(id+"F8.wireOp",EDGE,"E106.sketch_text.stroke-29"),sQuery(id+"F8.wireOp",EDGE,"E106.sketch_text.stroke-30"),sQuery(id+"F8.wireOp",EDGE,"E106.sketch_text.stroke-31"),sQuery(id+"F8.wireOp",EDGE,"E106.sketch_text.stroke-32"),sQuery(id+"F8.wireOp",EDGE,"E106.sketch_text.stroke-33"),sQuery(id+"F8.wireOp",EDGE,"E106.sketch_text.stroke-34"),sQuery(id+"F8.wireOp",EDGE,"E106.sketch_text.stroke-35"),sQuery(id+"F8.wireOp",EDGE,"E106.sketch_text.stroke-36"),sQuery(id+"F8.wireOp",EDGE,"E106.sketch_text.stroke-37"),sQuery(id+"F8.wireOp",EDGE,"E106.sketch_text.stroke-38"),sQuery(id+"F8.wireOp",EDGE,"E106.sketch_text.stroke-39"),sQuery(id+"F8.wireOp",EDGE,"E106.sketch_text.stroke-40"),sQuery(id+"F8.wireOp",EDGE,"E106.sketch_text.stroke-41"),sQuery(id+"F8.wireOp",EDGE,"E106.sketch_text.stroke-42")])],"isStart":false});
            var Q12;
            Q12=makeQuery(id+"F9.opExtrude","CAP_FACE",FACE,{"disambiguationData":[OSD([sQuery(id+"F8.wireOp",EDGE,"E106.sketch_text.stroke-57"),sQuery(id+"F8.wireOp",EDGE,"E106.sketch_text.stroke-58"),sQuery(id+"F8.wireOp",EDGE,"E106.sketch_text.stroke-59"),sQuery(id+"F8.wireOp",EDGE,"E106.sketch_text.stroke-60"),sQuery(id+"F8.wireOp",EDGE,"E106.sketch_text.stroke-61"),sQuery(id+"F8.wireOp",EDGE,"E106.sketch_text.stroke-62"),sQuery(id+"F8.wireOp",EDGE,"E106.sketch_text.stroke-63"),sQuery(id+"F8.wireOp",EDGE,"E106.sketch_text.stroke-64"),sQuery(id+"F8.wireOp",EDGE,"E106.sketch_text.stroke-65"),sQuery(id+"F8.wireOp",EDGE,"E106.sketch_text.stroke-66"),sQuery(id+"F8.wireOp",EDGE,"E106.sketch_text.stroke-67"),sQuery(id+"F8.wireOp",EDGE,"E106.sketch_text.stroke-68"),sQuery(id+"F8.wireOp",EDGE,"E106.sketch_text.stroke-69"),sQuery(id+"F8.wireOp",EDGE,"E106.sketch_text.stroke-70")])],"isStart":false});
            var Q13;
            Q13=makeQuery(id+"F9.opExtrude","CAP_FACE",FACE,{"disambiguationData":[OSD([sQuery(id+"F8.wireOp",EDGE,"E106.sketch_text.stroke-71"),sQuery(id+"F8.wireOp",EDGE,"E106.sketch_text.stroke-72"),sQuery(id+"F8.wireOp",EDGE,"E106.sketch_text.stroke-73"),sQuery(id+"F8.wireOp",EDGE,"E106.sketch_text.stroke-74"),sQuery(id+"F8.wireOp",EDGE,"E106.sketch_text.stroke-75"),sQuery(id+"F8.wireOp",EDGE,"E106.sketch_text.stroke-76"),sQuery(id+"F8.wireOp",EDGE,"E106.sketch_text.stroke-77"),sQuery(id+"F8.wireOp",EDGE,"E106.sketch_text.stroke-78"),sQuery(id+"F8.wireOp",EDGE,"E106.sketch_text.stroke-79"),sQuery(id+"F8.wireOp",EDGE,"E106.sketch_text.stroke-80"),sQuery(id+"F8.wireOp",EDGE,"E106.sketch_text.stroke-81"),sQuery(id+"F8.wireOp",EDGE,"E106.sketch_text.stroke-82"),sQuery(id+"F8.wireOp",EDGE,"E106.sketch_text.stroke-83"),sQuery(id+"F8.wireOp",EDGE,"E106.sketch_text.stroke-84"),sQuery(id+"F8.wireOp",EDGE,"E106.sketch_text.stroke-85"),sQuery(id+"F8.wireOp",EDGE,"E106.sketch_text.stroke-86"),sQuery(id+"F8.wireOp",EDGE,"E106.sketch_text.stroke-87"),sQuery(id+"F8.wireOp",EDGE,"E106.sketch_text.stroke-88"),sQuery(id+"F8.wireOp",EDGE,"E106.sketch_text.stroke-89")])],"isStart":false});
            var Q14;
            Q14=makeQuery(id+"F9.opExtrude","CAP_FACE",FACE,{"disambiguationData":[OSD([sQuery(id+"F8.wireOp",EDGE,"E106.sketch_text.stroke-43"),sQuery(id+"F8.wireOp",EDGE,"E106.sketch_text.stroke-44"),sQuery(id+"F8.wireOp",EDGE,"E106.sketch_text.stroke-45"),sQuery(id+"F8.wireOp",EDGE,"E106.sketch_text.stroke-46"),sQuery(id+"F8.wireOp",EDGE,"E106.sketch_text.stroke-47"),sQuery(id+"F8.wireOp",EDGE,"E106.sketch_text.stroke-48"),sQuery(id+"F8.wireOp",EDGE,"E106.sketch_text.stroke-49"),sQuery(id+"F8.wireOp",EDGE,"E106.sketch_text.stroke-50"),sQuery(id+"F8.wireOp",EDGE,"E106.sketch_text.stroke-51"),sQuery(id+"F8.wireOp",EDGE,"E106.sketch_text.stroke-52"),sQuery(id+"F8.wireOp",EDGE,"E106.sketch_text.stroke-53"),sQuery(id+"F8.wireOp",EDGE,"E106.sketch_text.stroke-54"),sQuery(id+"F8.wireOp",EDGE,"E106.sketch_text.stroke-55"),sQuery(id+"F8.wireOp",EDGE,"E106.sketch_text.stroke-56")])],"isStart":false});
            var Q15;
            Q15=makeQuery(id+"F9.opExtrude","CAP_FACE",FACE,{"disambiguationData":[OSD([sQuery(id+"F8.wireOp",EDGE,"E106.sketch_text.stroke-12"),sQuery(id+"F8.wireOp",EDGE,"E106.sketch_text.stroke-13"),sQuery(id+"F8.wireOp",EDGE,"E106.sketch_text.stroke-14"),sQuery(id+"F8.wireOp",EDGE,"E106.sketch_text.stroke-15"),sQuery(id+"F8.wireOp",EDGE,"E106.sketch_text.stroke-16"),sQuery(id+"F8.wireOp",EDGE,"E106.sketch_text.stroke-17")])],"isStart":false});
            var Q16;
            Q16=makeQuery(id+"F9.opExtrude","CAP_FACE",FACE,{"disambiguationData":[OSD([sQuery(id+"F8.wireOp",EDGE,"E106.sketch_text.stroke-82"),sQuery(id+"F8.wireOp",EDGE,"E106.sketch_text.stroke-83"),sQuery(id+"F8.wireOp",EDGE,"E106.sketch_text.stroke-84"),sQuery(id+"F8.wireOp",EDGE,"E106.sketch_text.stroke-85"),sQuery(id+"F8.wireOp",EDGE,"E106.sketch_text.stroke-86"),sQuery(id+"F8.wireOp",EDGE,"E106.sketch_text.stroke-87"),sQuery(id+"F8.wireOp",EDGE,"E106.sketch_text.stroke-88"),sQuery(id+"F8.wireOp",EDGE,"E106.sketch_text.stroke-89"),sQuery(id+"F8.wireOp",EDGE,"E106.sketch_text.stroke-90"),sQuery(id+"F8.wireOp",EDGE,"E106.sketch_text.stroke-91"),sQuery(id+"F8.wireOp",EDGE,"E106.sketch_text.stroke-92"),sQuery(id+"F8.wireOp",EDGE,"E106.sketch_text.stroke-93")])],"isStart":false});
            fillet(context, id + "F10", {"entities" : qUnion([Q0, Q1, Q2, Q3, Q4, Q5, Q6, Q7, Q8, Q9, Q10, Q11, Q12, Q13, Q14, Q15, Q16]), "radius" : 0.38 * mm, "tangentPropagation" : true, "allowEdgeOverflow" : false});
        }
    });
